# Revit family: Уні Макс_Eng
name_source: partatom
category: Mechanical Equipment
units: mm (PartAtom-declared; Revit-internal decimal feet)

## family parameters
Always vertical = Yes
Classification = None
Cut with Voids When Loaded = No
Part Type = Normal
Room Calculation Point = No
Round Connector Dimension = Use Diameter
Shared = No
Work Plane-Based = No

## types (4) — shared parameters
00_20_Manufacturer = Vents
00_20_Name = Centralised ventilation unit
A = 1070 mm  [stored 3.5105 ft]
B = 790 mm  [stored 2.59186 ft]
B1 = 730 mm  [stored 2.39501 ft]
Casing Material = Metal, painted, white, matte
D = 125 mm  [stored 0.410105 ft]
Description = For round channels
Diameter = 125 mm  [stored 0.410105 ft]
Dy = 121 mm  [stored 0.396982 ft]
Filter = F7/G4
Frequency = 50 Hz
H = 251 mm  [stored 0.823491 ft]
Height = 251 mm  [stored 0.823491 ft]
Length = 1070 mm  [stored 3.5105 ft]
Load Classification = HVAC
Maintenance zone material = <By Category>
Manufacturer = Vents
Maximum Air Flow = 160.0 m³/h
Number of Fase = 1
Sound pressure level at 3 m distance = 32 dBA
Temperature of moving air = –25…+40 °C
URL = https://ventilation-system.com
Voltage = 230 V
Weight = 47.00 kg
Width = 790 mm  [stored 2.59186 ft]
zero-valued in all types: Default Elevation

## per-type parameters (varying)
| type | Amperage | Bp | Grid Material | Lp | Power | Side | UP | UP_Side | alfa |
| Uni Max А21 | 1 A | 0 mm  [stored 0 ft] | Grid, painted, white | 151 mm  [stored 0.495407 ft] | 58 W | No | No | Yes | 90.00° |
| Uni Max Е А21 | 4 A | 460 mm  [stored 1.50919 ft] | Grid_slot, steel, painted, white | 195 mm  [stored 0.639764 ft] | 858 W | Yes | Yes | No | 0.00° |
| Uni Max ERV А21 | 1 A | 460 mm  [stored 1.50919 ft] | Grid_slot, steel, painted, white | 195 mm  [stored 0.639764 ft] | 58 W | Yes | Yes | No | 0.00° |
| Uni Max Е ERV А21 | 4 A | 460 mm  [stored 1.50919 ft] | Grid_slot, steel, painted, white | 195 mm  [stored 0.639764 ft] | 858 W | Yes | Yes | No | 0.00° |

note: column(s) folded — value = type name in every type: 00_20_Type

note: [stored X ft] marks values corroborated as IEEE doubles in the binary element streams (Revit-internal decimal feet)
